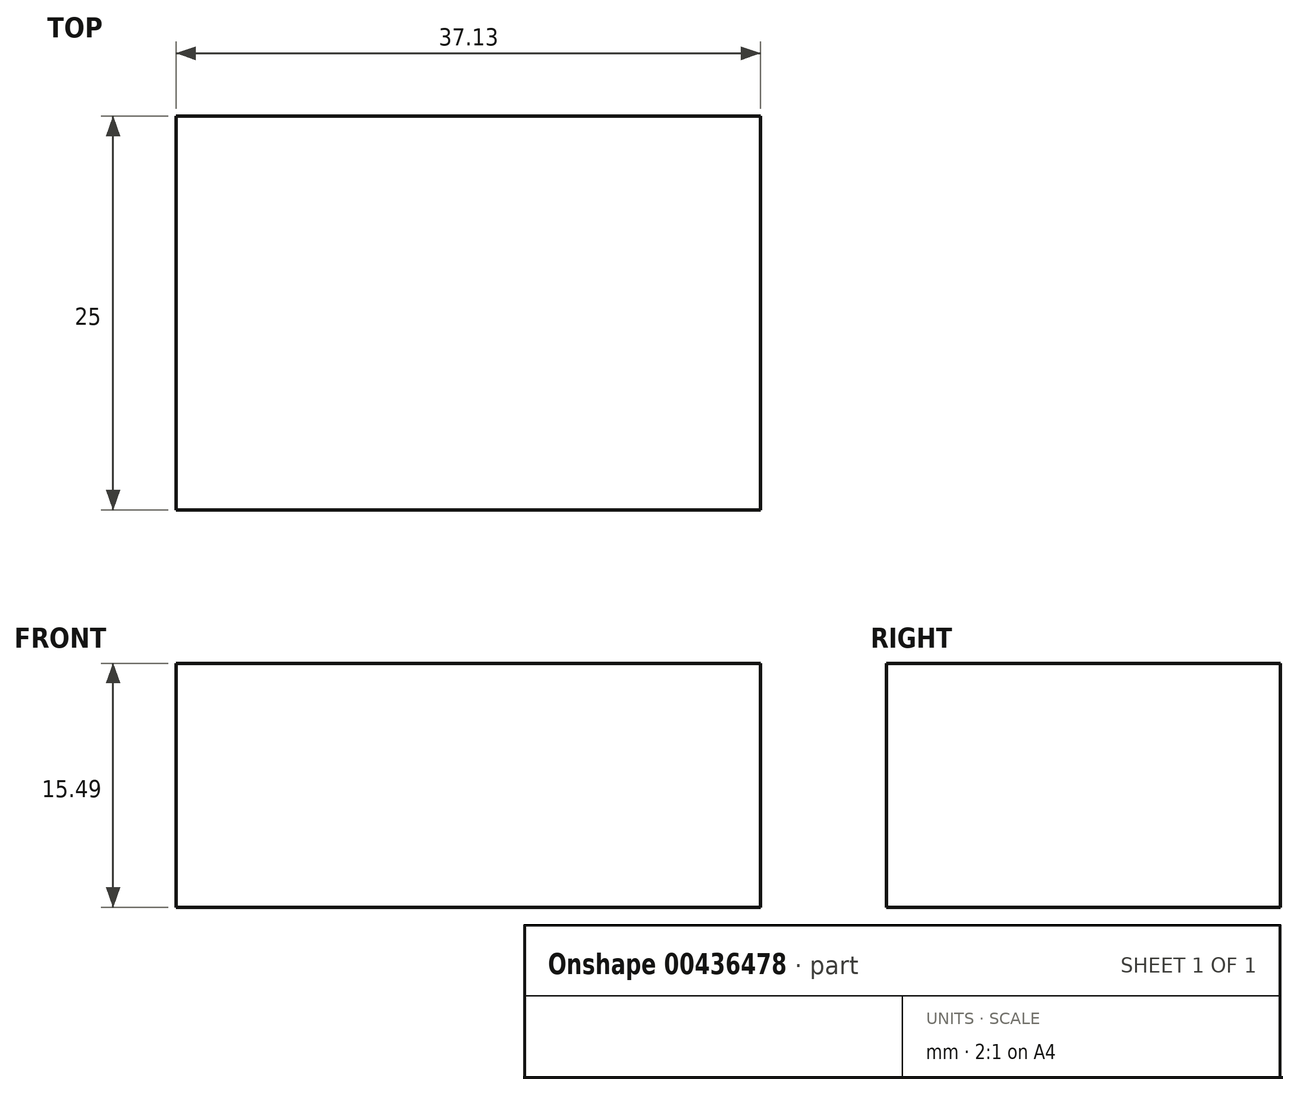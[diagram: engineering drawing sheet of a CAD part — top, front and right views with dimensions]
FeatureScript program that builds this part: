
annotation { "Feature Type Name" : "Feature", "Feature Type Description" : "" }
export const myFeature = defineFeature(function(context is Context, id is Id, definition is map)
    precondition{}
    {
        {
            var Q0;
            Q0=qCreatedBy(makeId("Front.planeOp"),FACE);
            var sketch = newSketch(context, id + "F0", { "sketchPlane" : qUnion([Q0])});
            skLineSegment(sketch, "E0.bottom", {"start": v(0, 0) * mm, "end": v(37.13, 0) * mm});
            skLineSegment(sketch, "E0.top", {"start": v(0, -15.49) * mm, "end": v(37.13, -15.49) * mm});
            skLineSegment(sketch, "E0.left", {"start": v(0, 0) * mm, "end": v(0, -15.49) * mm});
            skLineSegment(sketch, "E0.right", {"start": v(37.13, 0) * mm, "end": v(37.13, -15.49) * mm});
            skSolve(sketch);
        }
        {
            var Q0;
            Q0=makeQuery(id+"F0.imprint","IMPRINT",FACE,{"disambiguationData":[TD([[makeQuery(id+"F0.imprint","IMPRINT",EDGE,{"derivedFrom":sQuery(id+"F0.wireOp",EDGE,"E0.bottom")}),-1.0]])]});
            extrude(context, id + "F1", {"entities" : qUnion([Q0]), "depth" : 25 * mm});
        }
    });
